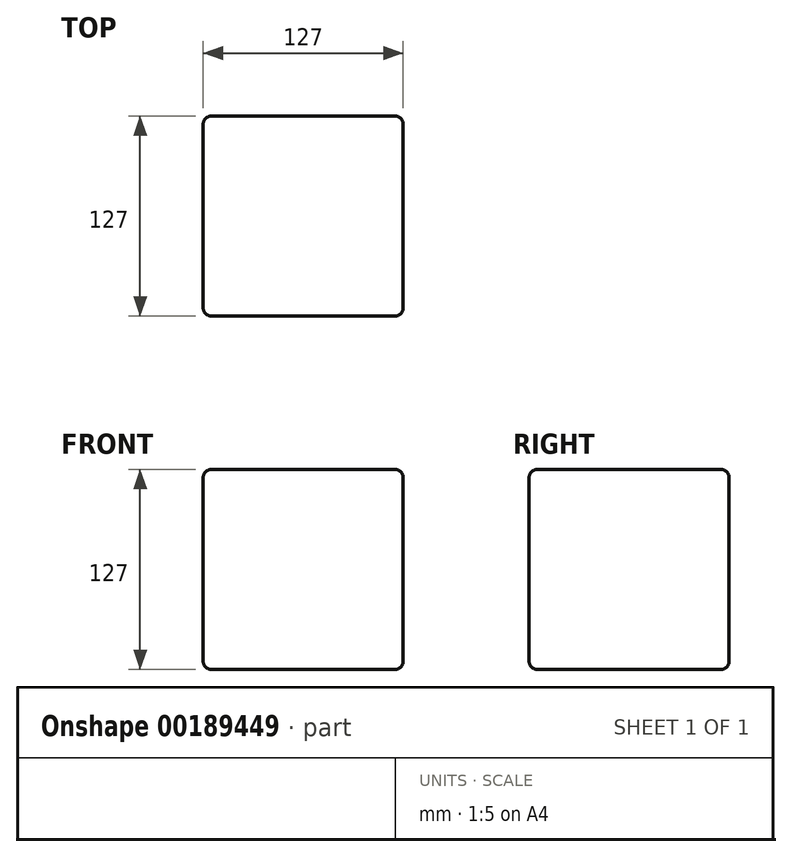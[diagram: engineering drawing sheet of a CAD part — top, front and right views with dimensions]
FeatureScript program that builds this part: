
annotation { "Feature Type Name" : "Feature", "Feature Type Description" : "" }
export const myFeature = defineFeature(function(context is Context, id is Id, definition is map)
    precondition{}
    {
        {
            var Q0;
            Q0=qCreatedBy(makeId("Front.planeOp"),FACE);
            var sketch = newSketch(context, id + "F0", { "sketchPlane" : qUnion([Q0])});
            skLineSegment(sketch, "E0.bottom", {"start": v(0, 0) * mm, "end": v(127, 0) * mm});
            skLineSegment(sketch, "E0.top", {"start": v(0, 127) * mm, "end": v(127, 127) * mm});
            skLineSegment(sketch, "E0.left", {"start": v(0, 0) * mm, "end": v(0, 127) * mm});
            skLineSegment(sketch, "E0.right", {"start": v(127, 0) * mm, "end": v(127, 127) * mm});
            skSolve(sketch);
        }
        {
            var Q0;
            Q0 = qSketchRegion(id + "F0", true);
            extrude(context, id + "F1", {"entities" : qUnion([Q0]), "endBound" : BoundingType.SYMMETRIC, "depth" : 127 * mm});
        }
        {
            var Q0;
            Q0=makeQuery(id+"F1.opExtrude","CAP_EDGE",EDGE,{"disambiguationData":[OSD([sQuery(id+"F0.wireOp",EDGE,"E0.top")])],"isStart":false});
            var Q1;
            Q1=makeQuery(id+"F1.opExtrude","SWEPT_EDGE",EDGE,{"disambiguationData":[OSD([sQuery(id+"F0.wireOp",EDGE,"E0.top"),sQuery(id+"F0.wireOp",EDGE,"E0.left")])]});
            var Q2;
            Q2=makeQuery(id+"F1.opExtrude","CAP_EDGE",EDGE,{"disambiguationData":[OSD([sQuery(id+"F0.wireOp",EDGE,"E0.left")])],"isStart":false});
            var Q3;
            Q3=makeQuery(id+"F1.opExtrude","CAP_EDGE",EDGE,{"disambiguationData":[OSD([sQuery(id+"F0.wireOp",EDGE,"E0.right")])],"isStart":false});
            var Q4;
            Q4=makeQuery(id+"F1.opExtrude","SWEPT_EDGE",EDGE,{"disambiguationData":[OSD([sQuery(id+"F0.wireOp",EDGE,"E0.top"),sQuery(id+"F0.wireOp",EDGE,"E0.right")])]});
            var Q5;
            Q5=makeQuery(id+"F1.opExtrude","SWEPT_FACE",FACE,{"disambiguationData":[OSD([sQuery(id+"F0.wireOp",EDGE,"E0.right")])]});
            var Q6;
            Q6=makeQuery(id+"F1.opExtrude","CAP_EDGE",EDGE,{"disambiguationData":[OSD([sQuery(id+"F0.wireOp",EDGE,"E0.top")])],"isStart":true});
            var Q7;
            Q7=makeQuery(id+"F1.opExtrude","CAP_FACE",FACE,{"disambiguationData":[OSD([sQuery(id+"F0.wireOp",EDGE,"E0.bottom"),sQuery(id+"F0.wireOp",EDGE,"E0.top"),sQuery(id+"F0.wireOp",EDGE,"E0.left"),sQuery(id+"F0.wireOp",EDGE,"E0.right")])],"isStart":true});
            var Q8;
            Q8=makeQuery(id+"F1.opExtrude","SWEPT_EDGE",EDGE,{"disambiguationData":[OSD([sQuery(id+"F0.wireOp",EDGE,"E0.bottom"),sQuery(id+"F0.wireOp",EDGE,"E0.left")])]});
            var Q9;
            Q9=makeQuery(id+"F1.opExtrude","CAP_FACE",FACE,{"disambiguationData":[OSD([sQuery(id+"F0.wireOp",EDGE,"E0.bottom"),sQuery(id+"F0.wireOp",EDGE,"E0.top"),sQuery(id+"F0.wireOp",EDGE,"E0.left"),sQuery(id+"F0.wireOp",EDGE,"E0.right")])],"isStart":false});
            fillet(context, id + "F2", {"entities" : qUnion([Q0, Q1, Q2, Q3, Q4, Q5, Q6, Q7, Q8, Q9]), "radius" : 5.08 * mm, "tangentPropagation" : true, "allowEdgeOverflow" : false});
        }
    });
